# Revit family: Little Petra VB1
name_source: partatom
category: Furniture
revit_build: Autodesk Revit 2017 (Build: 20171027_0315(x64)
units: mm (PartAtom-declared; Revit-internal decimal feet)

## family parameters
Always vertical = Yes
Cut with Voids When Loaded = No
OmniClass Number = 23.40.20.00
OmniClass Title = General Furniture and Specialties
Room Calculation Point = No
Shared = No
Work Plane-Based = No

## types (1)
- Little Petra VB1
    Base = &tradition White Oak Oiled Vertical
    Depth = 83cm/32.7in
    Description = Initially introduced back in 1938, Little Petra won instant praise at the Copenhagen Cabinetmakers Guild Exhibition, subsequently winning awards at exhibits in New York and Berlin.
    Design = Viggo Boesen
    Design Year = 1938
    Gliders = &tradition Felt Black
    Height = 75cm/29.2i
    Manufacturer = &tradition
    Model = Little Petra VB1
    Packaging Dimensions = H: 78cm/30.7in, D: 85cm/33.5in, L: 85cm/33.5in
    Seat Height = 40cm/15.8in
    Shell = &tradition Hallingdal 130
    Type Comments = Little Petra Series
    URL = https://www.andtradition.com
    Variation Upholsthery = Available in Karakorum 003, Sheepskin Moonlight or Sheepskin Sahara. Other fabric available upon request.
    Variations Base = Available in Oiled Oak
    Weight = 20kg
    Width = 79cm/31.1in

## geometry (parser evidence)
native form markers: Sweep x3
no freeform markers — native parametric forms only
